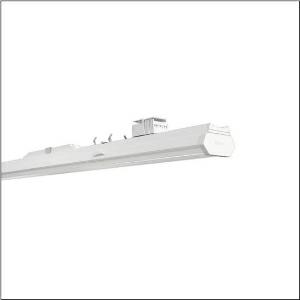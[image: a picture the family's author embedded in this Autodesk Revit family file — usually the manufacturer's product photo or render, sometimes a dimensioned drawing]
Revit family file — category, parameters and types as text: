
# Revit family: licross_11_protected_ho_51td12dn4fxm3s4
name_source: partatom
category: Lighting Fixtures
units: mm (PartAtom-declared; Revit-internal decimal feet)

## family parameters
Cut with Voids When Loaded = No
Host = Face
Light Source = No
Part Type = Normal
Room Calculation Point = No
Round Connector Dimension = Use Diameter
Shared = No

## types (1)
- --- (1 x LED, 970 lm, 7.4 W, 4000K)
    Apparent Load = 7 VA
    CIE Flux Codes = 70 91 97 98 100
    Color Rendering = 80
    Color Temperature = 4000K
    Default Elevation = 1800 mm
    Description = Licross 11 Protected HO, luminaire insert, of sheet steel, galvanised, coil coated, white, length: 1.500mm, width: 90mm, height: 101mm, LED rated luminous flux: 15.270lm, light colour: 840, SDCM (Standard Deviation of Colour Matching)MacAdam ≤ 2 SDCM (initial), control gear: DALI 2, with plug, 6-pole, with phase selection, for trunking rail, 9 or 11-core, mains connection: 220..240V, AC, 50/60Hz, rated input power: 91W, for trunking rail, 9-/11-core, internal wiring halogen-free, for emergency light function, converter,control gear: single battery element, battery: LiFePO4, 9Ah, primary light control with lens, of plastic, primary optical cover: cover, of PMMA, light emission: direct distribution, primary light characteristic: symmetric, protection rating (complete): IP54, insulation class (complete): insulation class I (protective earthing), certification: CE, UKCA, protection symbol: D if used in an environment with non-conductive dust loads with corresponding accessories, impact resistance: IK06, permissible ambient temperature for indoor applications: +5..+30°C, standard: EN 60598-2-22, LABS conformity tested according to VDMA 24364:2018-05, reducing of maximum allowable ambient temperature of 5°C with ceiling mounting, corresponds to IFS (International Featured Standards) requirements for safety and quality in the food industry, The light source and the operating device comply with the requirements of the Ecodesign Regulation (EU) 2019/2020 and are replaceable in accordance with this regulation, packaging unit: 1 piece
    Height = 92 mm
    Lamp = 1 x LED
    Lamp Light Flux = 970 lm
    Lamp Power = 7.4 W
    Lamp count = 1
    Length = 1500 mm
    Luminous efficacy = 131 lm/W
    Manufacturer = Siteco
    ModVariant = No
    Model = 51TD12DN4FXM3S4
    Mounting Place = Ceiling
    Mounting Type = Pendant
    Number of Poles = 1
    OnlyDefault = Yes
    Power Factor = 1
    Product Name = Licross 11 Protected HO
    Product group = luminaire insert | ceiling pendant
    ProductGroupID = 901
    Protection Class = Protection class I
    Protection Degree = IP 54
    RLX_Detail_Level = 1
    RLX_Emergency_Light_Flux = 0 lm
    RLX_Emergency_Type = 0
    RLX_Emergency_Type_DB = No
    RlxData = <blob elided: 25145 chars, md5=c7fa16a2>
    Socket = socket
    Standby Power = 0 W
    System Light Flux = 970 lm
    System Power = 7 W
    Type Comments = : emergency light operation: 3 h
    Type Image = l_1256145.jpg
    URL = http://relux.com
    VarID = @adj_094701
    Voltage = 0 V
    Weight = 0.00 kg
    Width = 88 mm

## geometry (parser evidence)
native form markers: Blend x4, Sweep x9
no freeform markers — native parametric forms only
